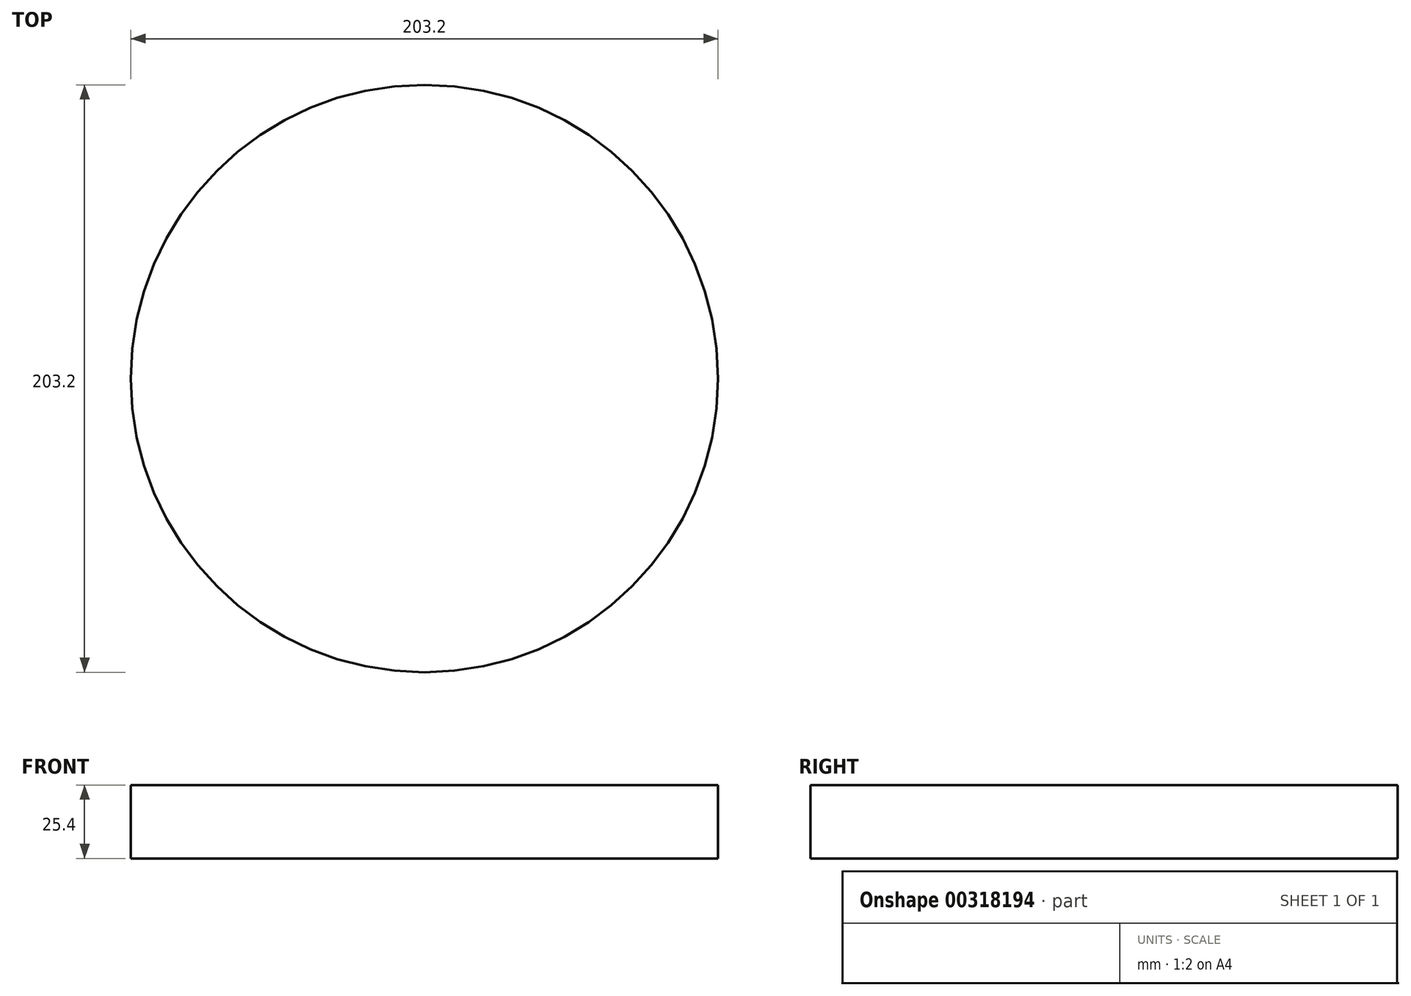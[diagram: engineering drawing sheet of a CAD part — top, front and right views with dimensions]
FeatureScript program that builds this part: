
annotation { "Feature Type Name" : "Feature", "Feature Type Description" : "" }
export const myFeature = defineFeature(function(context is Context, id is Id, definition is map)
    precondition{}
    {
        {
            var Q0;
            Q0=qCreatedBy(makeId("Top.planeOp"),FACE);
            var sketch = newSketch(context, id + "F0", { "sketchPlane" : qUnion([Q0])});
            skCircle(sketch, "E0", {"center": v(0, 0) * mm, "radius": 101.6 * mm});
            skSolve(sketch);
        }
        {
            var Q0;
            Q0 = qSketchRegion(id + "F0", true);
            extrude(context, id + "F1", {"entities" : qUnion([Q0]), "depth" : 25.4 * mm});
        }
    });
